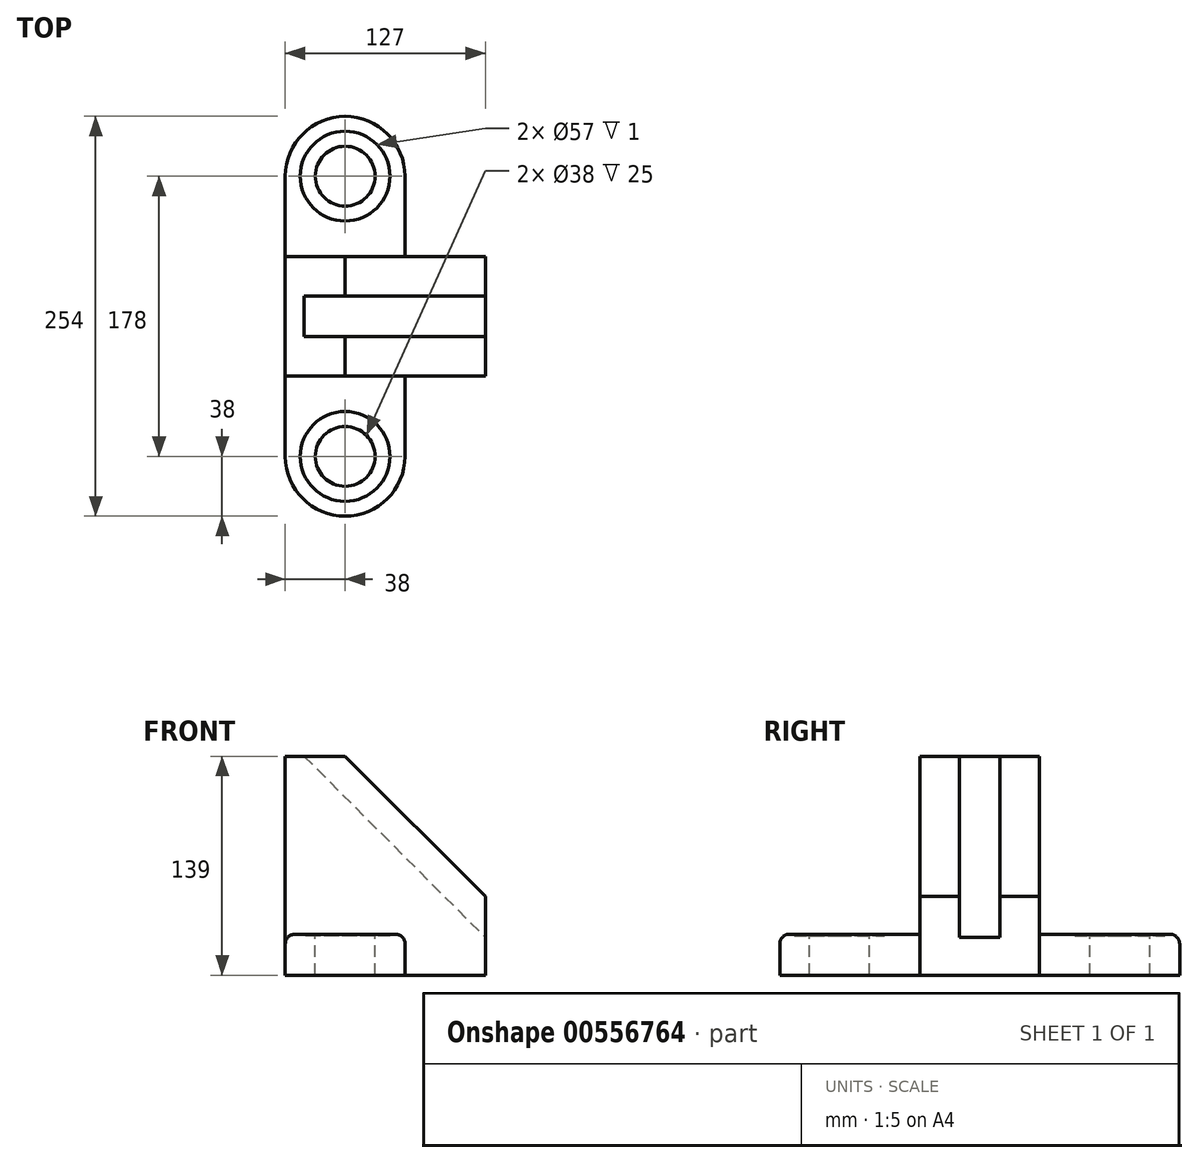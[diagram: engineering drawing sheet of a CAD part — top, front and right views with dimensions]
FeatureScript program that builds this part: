
annotation { "Feature Type Name" : "Feature", "Feature Type Description" : "" }
export const myFeature = defineFeature(function(context is Context, id is Id, definition is map)
    precondition{}
    {
        {
            var Q0;
            Q0=qCreatedBy(makeId("Top.planeOp"),FACE);
            var sketch = newSketch(context, id + "F0", { "sketchPlane" : qUnion([Q0])});
            skLineSegment(sketch, "E0.bottom", {"start": v(0, 0) * mm, "end": v(127, 0) * mm});
            skLineSegment(sketch, "E0.top", {"start": v(0, 76) * mm, "end": v(127, 76) * mm});
            skLineSegment(sketch, "E0.left", {"start": v(0, 0) * mm, "end": v(0, 76) * mm});
            skLineSegment(sketch, "E0.right", {"start": v(127, 0) * mm, "end": v(127, 76) * mm});
            skSolve(sketch);
        }
        {
            var Q0;
            Q0=makeQuery(id+"F0.imprint","IMPRINT",FACE,{"disambiguationData":[TD([[makeQuery(id+"F0.imprint","IMPRINT",EDGE,{"derivedFrom":sQuery(id+"F0.wireOp",EDGE,"E0.bottom")}),1.0]])]});
            extrude(context, id + "F1", {"entities" : qUnion([Q0]), "depth" : 139 * mm, "offsetDistance" : 25 * mm});
        }
        {
            var Q0;
            Q0=makeQuery(id+"F1.opExtrude","SWEPT_FACE",FACE,{"disambiguationData":[OSD([sQuery(id+"F0.wireOp",EDGE,"E0.bottom")])]});
            var sketch = newSketch(context, id + "F2", { "sketchPlane" : qUnion([Q0])});
            skLineSegment(sketch, "E1", {"start": v(38, 139) * mm, "end": v(127, 50) * mm});
            skSolve(sketch);
        }
        {
            var Q0;
            {var subQ0=sQuery(id+"F2.wireOp",EDGE,"E1");Q0=makeQuery(id+"F2.imprint","IMPRINT",FACE,{"disambiguationData":[TD([[makeQuery(id+"F2.imprint","IMPRINT",EDGE,{"derivedFrom":subQ0}),1.0]])]});}
            extrude(context, id + "F3", {"entities" : qUnion([Q0]), "operationType" : NewBodyOperationType.REMOVE, "endBound" : BoundingType.THROUGH_ALL, "oppositeDirection" : true, "depth" : 25 * mm, "offsetDistance" : 25 * mm});
        }
        {
            var Q0;
            Q0=makeQuery(id+"F1.opExtrude","CAP_FACE",FACE,{"disambiguationData":[OSD([sQuery(id+"F0.wireOp",EDGE,"E0.bottom"),sQuery(id+"F0.wireOp",EDGE,"E0.top"),sQuery(id+"F0.wireOp",EDGE,"E0.left"),sQuery(id+"F0.wireOp",EDGE,"E0.right")])],"isStart":false});
            var sketch = newSketch(context, id + "F4", { "sketchPlane" : qUnion([Q0])});
            skLineSegment(sketch, "E2.bottom", {"start": v(38, 25) * mm, "end": v(12, 25) * mm});
            skLineSegment(sketch, "E2.top", {"start": v(38, 51) * mm, "end": v(12, 51) * mm});
            skLineSegment(sketch, "E2.left", {"start": v(38, 25) * mm, "end": v(38, 51) * mm});
            skLineSegment(sketch, "E2.right", {"start": v(12, 25) * mm, "end": v(12, 51) * mm});
            skSolve(sketch);
        }
        {
            var Q0;
            Q0=makeQuery(id+"F1.opExtrude","SWEPT_FACE",FACE,{"disambiguationData":[OSD([sQuery(id+"F0.wireOp",EDGE,"E0.bottom")])]});
            var sketch = newSketch(context, id + "F5", { "sketchPlane" : qUnion([Q0])});
            skLineSegment(sketch, "E3", {"start": v(12, 139) * mm, "end": v(127, 24) * mm});
            skSolve(sketch);
        }
        {
            var Q0;
            Q0=makeQuery(id+"F4.imprint","IMPRINT",FACE,{"disambiguationData":[TD([[makeQuery(id+"F4.imprint","IMPRINT",EDGE,{"derivedFrom":sQuery(id+"F4.wireOp",EDGE,"E2.bottom")}),-1.0]])]});
            var Q1;
            Q1=sQuery(id+"F5.wireOp",EDGE,"E3");
            sweep(context, id + "F6", {"operationType" : NewBodyOperationType.REMOVE, "profiles" : qUnion([Q0]), "path" : qUnion([Q1])});
        }
        {
            var Q0;
            Q0=qCreatedBy(makeId("Top.planeOp"),FACE);
            var sketch = newSketch(context, id + "F7", { "sketchPlane" : qUnion([Q0])});
            skLineSegment(sketch, "E4.bottom", {"start": v(0, 0) * mm, "end": v(76, 0) * mm});
            skLineSegment(sketch, "E4.top", {"start": v(0, -51) * mm, "end": v(76, -51) * mm});
            skLineSegment(sketch, "E4.left", {"start": v(0, 0) * mm, "end": v(0, -51) * mm});
            skLineSegment(sketch, "E4.right", {"start": v(76, 0) * mm, "end": v(76, -51) * mm});
            skArc(sketch, "E5", {"start": v(76, -51) * mm, "mid": v(38, -89) * mm, "end": v(0, -51) * mm});
            skSolve(sketch);
        }
        {
            var Q0;
            Q0=makeQuery(id+"F7.imprint","IMPRINT",FACE,{"disambiguationData":[TD([[makeQuery(id+"F7.imprint","IMPRINT",EDGE,{"derivedFrom":sQuery(id+"F7.wireOp",EDGE,"E4.top")}),-1.0]])]});
            var Q1;
            Q1=makeQuery(id+"F7.imprint","IMPRINT",FACE,{"disambiguationData":[TD([[makeQuery(id+"F7.imprint","IMPRINT",EDGE,{"derivedFrom":sQuery(id+"F7.wireOp",EDGE,"E4.bottom")}),-1.0]])]});
            extrude(context, id + "F8", {"entities" : qUnion([Q0, Q1]), "operationType" : NewBodyOperationType.ADD, "depth" : 26 * mm, "offsetDistance" : 25 * mm});
        }
        {
            var Q0;
            Q0=makeQuery(id+"F8.boolean.opBoolean","MERGE",FACE,{"derivedFrom":[makeQuery(id+"F1.opExtrude","CAP_FACE",FACE,{"disambiguationData":[OSD([sQuery(id+"F0.wireOp",EDGE,"E0.bottom"),sQuery(id+"F0.wireOp",EDGE,"E0.top"),sQuery(id+"F0.wireOp",EDGE,"E0.left"),sQuery(id+"F0.wireOp",EDGE,"E0.right")])],"isStart":true}),makeQuery(id+"F8.opExtrude","CAP_FACE",FACE,{"disambiguationData":[OSD([sQuery(id+"F7.wireOp",EDGE,"E4.bottom"),sQuery(id+"F7.wireOp",EDGE,"E4.left"),sQuery(id+"F7.wireOp",EDGE,"E4.right"),sQuery(id+"F7.wireOp",EDGE,"E5")])],"isStart":true})]});
            var sketch = newSketch(context, id + "F9", { "sketchPlane" : qUnion([Q0])});
            skLineSegment(sketch, "E6.bottom", {"start": v(0, -76) * mm, "end": v(76, -76) * mm});
            skLineSegment(sketch, "E6.top", {"start": v(0, -127) * mm, "end": v(76, -127) * mm});
            skLineSegment(sketch, "E6.left", {"start": v(0, -76) * mm, "end": v(0, -127) * mm});
            skLineSegment(sketch, "E6.right", {"start": v(76, -76) * mm, "end": v(76, -127) * mm});
            skArc(sketch, "E7", {"start": v(0, -127) * mm, "mid": v(38, -165) * mm, "end": v(76, -127) * mm});
            skSolve(sketch);
        }
        {
            var Q0;
            Q0=makeQuery(id+"F9.imprint","IMPRINT",FACE,{"disambiguationData":[TD([[makeQuery(id+"F9.imprint","IMPRINT",EDGE,{"derivedFrom":sQuery(id+"F9.wireOp",EDGE,"E6.top")}),-1.0]])]});
            var Q1;
            Q1=makeQuery(id+"F9.imprint","IMPRINT",FACE,{"disambiguationData":[TD([[makeQuery(id+"F9.imprint","IMPRINT",EDGE,{"derivedFrom":sQuery(id+"F9.wireOp",EDGE,"E6.bottom")}),-1.0]])]});
            extrude(context, id + "F10", {"entities" : qUnion([Q0, Q1]), "operationType" : NewBodyOperationType.ADD, "oppositeDirection" : true, "depth" : 26 * mm, "offsetDistance" : 25 * mm});
        }
        {
            var Q0;
            Q0=makeQuery(id+"F8.opExtrude","CAP_EDGE",EDGE,{"disambiguationData":[OSD([sQuery(id+"F7.wireOp",EDGE,"E4.left")])],"isStart":false});
            fillet(context, id + "F11", {"entities" : qUnion([Q0]), "radius" : 6 * mm, "tangentPropagation" : true, "allowEdgeOverflow" : false});
        }
        {
            var Q0;
            Q0=makeQuery(id+"F10.opExtrude","CAP_EDGE",EDGE,{"disambiguationData":[OSD([sQuery(id+"F9.wireOp",EDGE,"E6.left")])],"isStart":false});
            fillet(context, id + "F12", {"entities" : qUnion([Q0]), "radius" : 6 * mm, "tangentPropagation" : true, "allowEdgeOverflow" : false});
        }
        {
            var Q0;
            Q0=makeQuery(id+"F8.opExtrude","CAP_FACE",FACE,{"disambiguationData":[OSD([sQuery(id+"F7.wireOp",EDGE,"E4.bottom"),sQuery(id+"F7.wireOp",EDGE,"E4.left"),sQuery(id+"F7.wireOp",EDGE,"E4.right"),sQuery(id+"F7.wireOp",EDGE,"E5")])],"isStart":false});
            var sketch = newSketch(context, id + "F13", { "sketchPlane" : qUnion([Q0])});
            skCircle(sketch, "E8", {"center": v(38, -51) * mm, "radius": 28.5 * mm});
            skSolve(sketch);
        }
        {
            var Q0;
            Q0=makeQuery(id+"F13.imprint","IMPRINT",FACE,{"disambiguationData":[TD([[makeQuery(id+"F13.imprint","IMPRINT",EDGE,{"derivedFrom":sQuery(id+"F13.wireOp",EDGE,"E8")}),1.0]])]});
            extrude(context, id + "F14", {"entities" : qUnion([Q0]), "operationType" : NewBodyOperationType.REMOVE, "oppositeDirection" : true, "depth" : 1 * mm, "offsetDistance" : 25 * mm});
        }
        {
            var Q0;
            Q0=makeQuery(id+"F14.boolean.opBoolean","COPY",FACE,{"derivedFrom":makeQuery(id+"F14.opExtrude","CAP_FACE",FACE,{"disambiguationData":[OSD([sQuery(id+"F13.wireOp",EDGE,"E8")])],"isStart":false})});
            var sketch = newSketch(context, id + "F15", { "sketchPlane" : qUnion([Q0])});
            skCircle(sketch, "E9", {"center": v(38, -51) * mm, "radius": 19 * mm});
            skSolve(sketch);
        }
        {
            var Q0;
            Q0=makeQuery(id+"F15.imprint","IMPRINT",FACE,{"disambiguationData":[TD([[makeQuery(id+"F15.imprint","IMPRINT",EDGE,{"derivedFrom":sQuery(id+"F15.wireOp",EDGE,"E9")}),1.0]])]});
            extrude(context, id + "F16", {"entities" : qUnion([Q0]), "operationType" : NewBodyOperationType.REMOVE, "endBound" : BoundingType.THROUGH_ALL, "oppositeDirection" : true, "depth" : 25 * mm, "offsetDistance" : 25 * mm});
        }
        {
            var Q0;
            Q0=makeQuery(id+"F10.opExtrude","CAP_FACE",FACE,{"disambiguationData":[OSD([sQuery(id+"F9.wireOp",EDGE,"E6.bottom"),sQuery(id+"F9.wireOp",EDGE,"E6.left"),sQuery(id+"F9.wireOp",EDGE,"E6.right"),sQuery(id+"F9.wireOp",EDGE,"E7")])],"isStart":false});
            var sketch = newSketch(context, id + "F17", { "sketchPlane" : qUnion([Q0])});
            skCircle(sketch, "E10", {"center": v(38, 127) * mm, "radius": 28.5 * mm});
            skSolve(sketch);
        }
        {
            var Q0;
            Q0=makeQuery(id+"F17.imprint","IMPRINT",FACE,{"disambiguationData":[TD([[makeQuery(id+"F17.imprint","IMPRINT",EDGE,{"derivedFrom":sQuery(id+"F17.wireOp",EDGE,"E10")}),1.0]])]});
            extrude(context, id + "F18", {"entities" : qUnion([Q0]), "operationType" : NewBodyOperationType.REMOVE, "oppositeDirection" : true, "depth" : 1 * mm, "offsetDistance" : 25 * mm});
        }
        {
            var Q0;
            Q0=makeQuery(id+"F18.boolean.opBoolean","COPY",FACE,{"derivedFrom":makeQuery(id+"F18.opExtrude","CAP_FACE",FACE,{"disambiguationData":[OSD([sQuery(id+"F17.wireOp",EDGE,"E10")])],"isStart":false})});
            var sketch = newSketch(context, id + "F19", { "sketchPlane" : qUnion([Q0])});
            skCircle(sketch, "E11", {"center": v(38, 127) * mm, "radius": 19 * mm});
            skSolve(sketch);
        }
        {
            var Q0;
            Q0=makeQuery(id+"F19.imprint","IMPRINT",FACE,{"disambiguationData":[TD([[makeQuery(id+"F19.imprint","IMPRINT",EDGE,{"derivedFrom":sQuery(id+"F19.wireOp",EDGE,"E11")}),1.0]])]});
            extrude(context, id + "F20", {"entities" : qUnion([Q0]), "operationType" : NewBodyOperationType.REMOVE, "endBound" : BoundingType.THROUGH_ALL, "oppositeDirection" : true, "depth" : 25 * mm, "offsetDistance" : 25 * mm});
        }
    });
